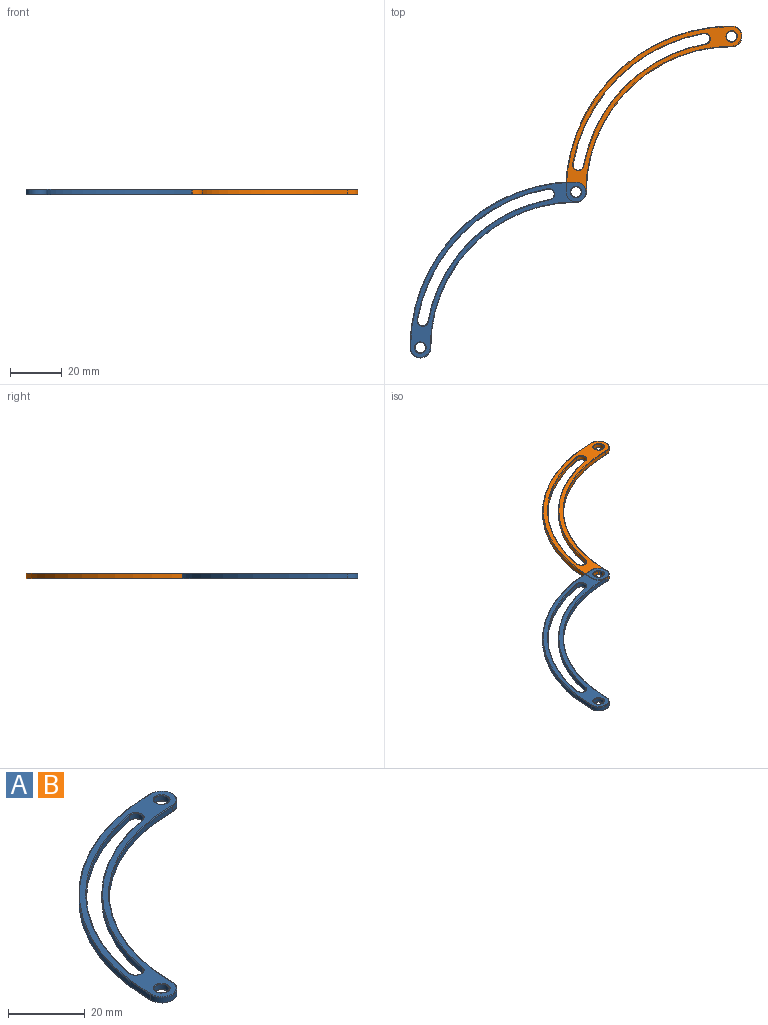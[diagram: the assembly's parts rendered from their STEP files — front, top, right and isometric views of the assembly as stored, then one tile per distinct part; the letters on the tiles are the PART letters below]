
ASSEMBLY  parts=2 mates=1
PART A: 32 faces, bbox 73.6x73.6x2 mm
  f0: cylinder r=4mm len=8mm, axis (0,0,-1), area 20.1mm2, adj f1,f9,f14,f24
  f1: cylinder r=64mm len=64mm, axis (0,0,-1), area 160.8mm2, adj f0,f2,f15,f25
  f2: cylinder r=4mm len=8mm, axis (0,0,-1), area 20.1mm2, adj f1,f9,f17,f27
  f3: cylinder r=62mm len=50.29mm, axis (0,0,-1), area 121.2mm2, adj f4,f6,f19,f29
  f4: cylinder r=2mm len=3.97mm, axis (0,0,-1), area 10.1mm2, adj f3,f5,f18,f28
  f5: cylinder r=58mm len=47.05mm, axis (0,0,-1), area 113.4mm2, adj f4,f6,f20,f30
  f6: cylinder r=2mm len=3.97mm, axis (0,0,-1), area 10.1mm2, adj f3,f5,f21,f31
  f7: cylinder r=2mm len=4mm, axis (0,0,-1), area 20.1mm2, adj f13,f23
  f8: cylinder r=2mm len=4mm, axis (0,0,-1), area 20.1mm2, adj f12,f22
  f9: cylinder r=56mm len=56mm, axis (0,0,-1), area 140.7mm2, adj f0,f2,f16,f26
  f10: plane 67.6x67.6mm, normal (0,0,1), area 393.5mm2, adj f22,f23,f24,f25,f26,f27,f28,f29
  f11: plane 67.6x67.6mm, normal (0,0,-1), area 393.5mm2, adj f12,f13,f14,f15,f16,f17,f18,f19
  f12: torus R=2.2mm, axis (0,0,1), area 4.1mm2, adj f8,f11
  f13: torus R=2.2mm, axis (0,0,1), area 4.1mm2, adj f7,f11
  f14: torus R=3.8mm, axis (0,0,1), area 3.9mm2, adj f0,f11,f15,f16
  f15: torus R=63.8mm, axis (0,0,1), area 31.5mm2, adj f1,f11,f14,f17
  f16: torus R=56.2mm, axis (0,0,1), area 27.7mm2, adj f9,f11,f14,f17
  f17: torus R=3.8mm, axis (0,0,1), area 3.9mm2, adj f2,f11,f15,f16
  f18: torus R=2.2mm, axis (0,0,1), area 2mm2, adj f4,f11,f19,f20
  f19: torus R=62.2mm, axis (0,0,1), area 23.8mm2, adj f3,f11,f18,f21
  f20: torus R=57.8mm, axis (0,0,1), area 22.2mm2, adj f5,f11,f18,f21
  f21: torus R=2.2mm, axis (0,0,1), area 2mm2, adj f6,f11,f19,f20
  f22: torus R=2.2mm, axis (0,0,1), area 4.1mm2, adj f8,f10
  f23: torus R=2.2mm, axis (0,0,1), area 4.1mm2, adj f7,f10
  f24: torus R=3.8mm, axis (0,0,1), area 3.9mm2, adj f0,f10,f25,f26
  f25: torus R=63.8mm, axis (0,0,1), area 31.5mm2, adj f1,f10,f24,f27
  f26: torus R=56.2mm, axis (0,0,1), area 27.7mm2, adj f9,f10,f24,f27
  f27: torus R=3.8mm, axis (0,0,1), area 3.9mm2, adj f2,f10,f25,f26
  f28: torus R=2.2mm, axis (0,0,1), area 2mm2, adj f4,f10,f29,f30
  f29: torus R=62.2mm, axis (0,0,1), area 23.8mm2, adj f3,f10,f28,f31
  f30: torus R=57.8mm, axis (0,0,1), area 22.2mm2, adj f5,f10,f28,f31
  f31: torus R=2.2mm, axis (0,0,1), area 2mm2, adj f6,f10,f29,f30
PART B: same geometry as A
PLACE A t=(-20.2,-102.98,36.36)mm
PLACE B t=(39.8,-42.98,36.36)mm
MATE revolute B.f8 <-> A.f7  axis (0,0,-1) through (-20.2,-42.98,38.16)mm
